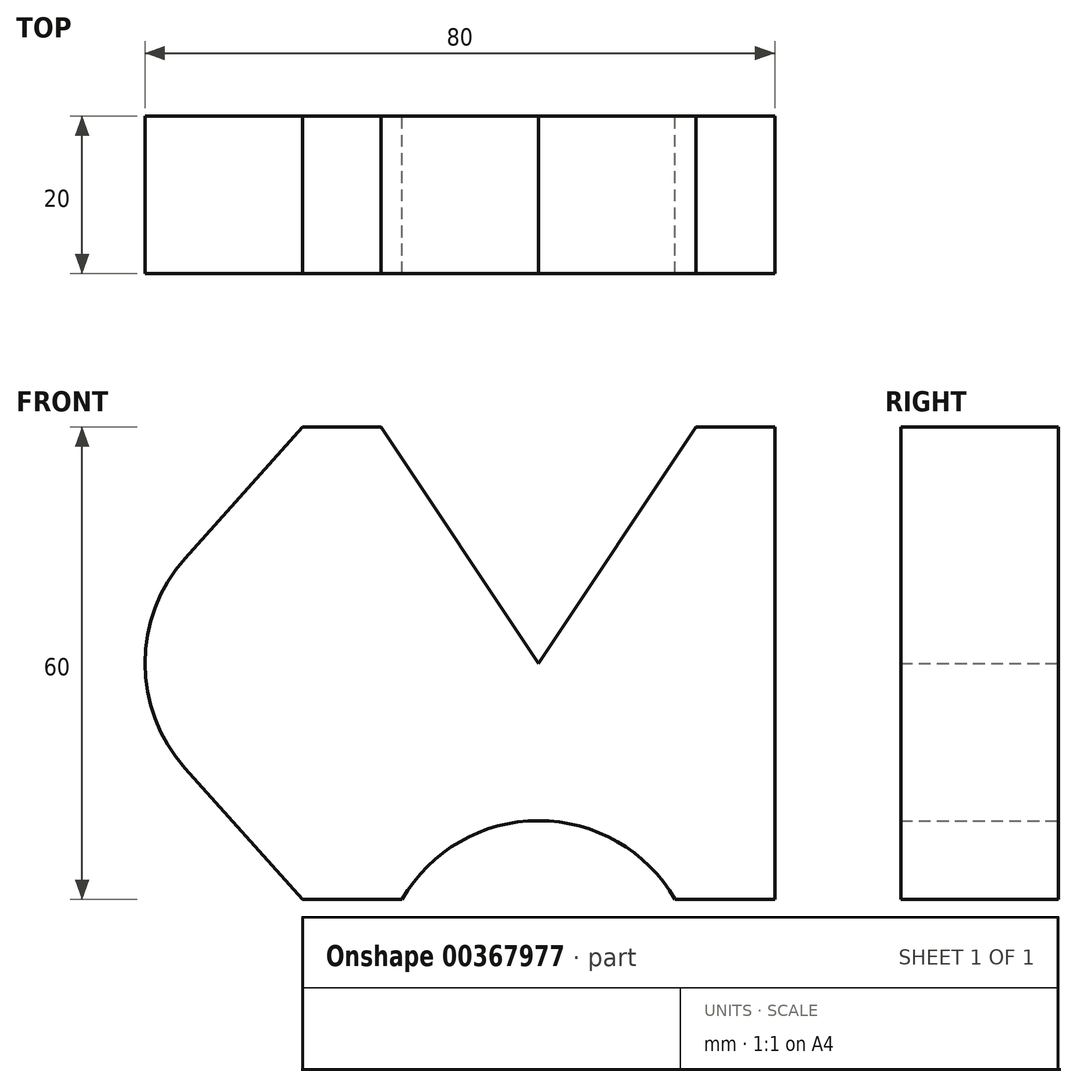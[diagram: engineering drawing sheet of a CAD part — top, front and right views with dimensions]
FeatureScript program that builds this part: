
annotation { "Feature Type Name" : "Feature", "Feature Type Description" : "" }
export const myFeature = defineFeature(function(context is Context, id is Id, definition is map)
    precondition{}
    {
        {
            var Q0;
            Q0=qCreatedBy(makeId("Front.planeOp"),FACE);
            var sketch = newSketch(context, id + "F0", { "sketchPlane" : qUnion([Q0])});
            skLineSegment(sketch, "E0", {"start": v(30, -30) * mm, "end": v(30, 0) * mm});
            skLineSegment(sketch, "E1", {"start": v(30, 30) * mm, "end": v(30, 0) * mm});
            skLineSegment(sketch, "E2", {"start": v(30, 30) * mm, "end": v(20, 30) * mm});
            skLineSegment(sketch, "E3", {"start": v(20, 30) * mm, "end": v(0, 0) * mm});
            skLineSegment(sketch, "E4", {"start": v(0, 0) * mm, "end": v(-20, 30) * mm});
            skLineSegment(sketch, "E5", {"start": v(-20, 30) * mm, "end": v(-30, 30) * mm});
            skLineSegment(sketch, "E6", {"start": v(-30, 30) * mm, "end": v(-44.9, 13.33) * mm});
            skArc(sketch, "E7", {"start": v(-44.9, 13.33) * mm, "mid": v(-50, 0) * mm, "end": v(-44.9, -13.33) * mm});
            skLineSegment(sketch, "E8", {"start": v(-44.9, -13.33) * mm, "end": v(-30, -30) * mm});
            skLineSegment(sketch, "E9", {"start": v(-30, -30) * mm, "end": v(-17.32, -30) * mm});
            skArc(sketch, "E10", {"start": v(17.32, -30) * mm, "mid": v(0, -20) * mm, "end": v(-17.32, -30) * mm});
            skLineSegment(sketch, "E11", {"start": v(17.32, -30) * mm, "end": v(30, -30) * mm});
            skLineSegment(sketch, "E12", {"start": v(-30, 30) * mm, "end": v(-30, -30) * mm, "construction": true});
            skSolve(sketch);
        }
        {
            var Q0;
            Q0 = qSketchRegion(id + "F0", true);
            extrude(context, id + "F1", {"entities" : qUnion([Q0]), "depth" : 20 * mm});
        }
    });
